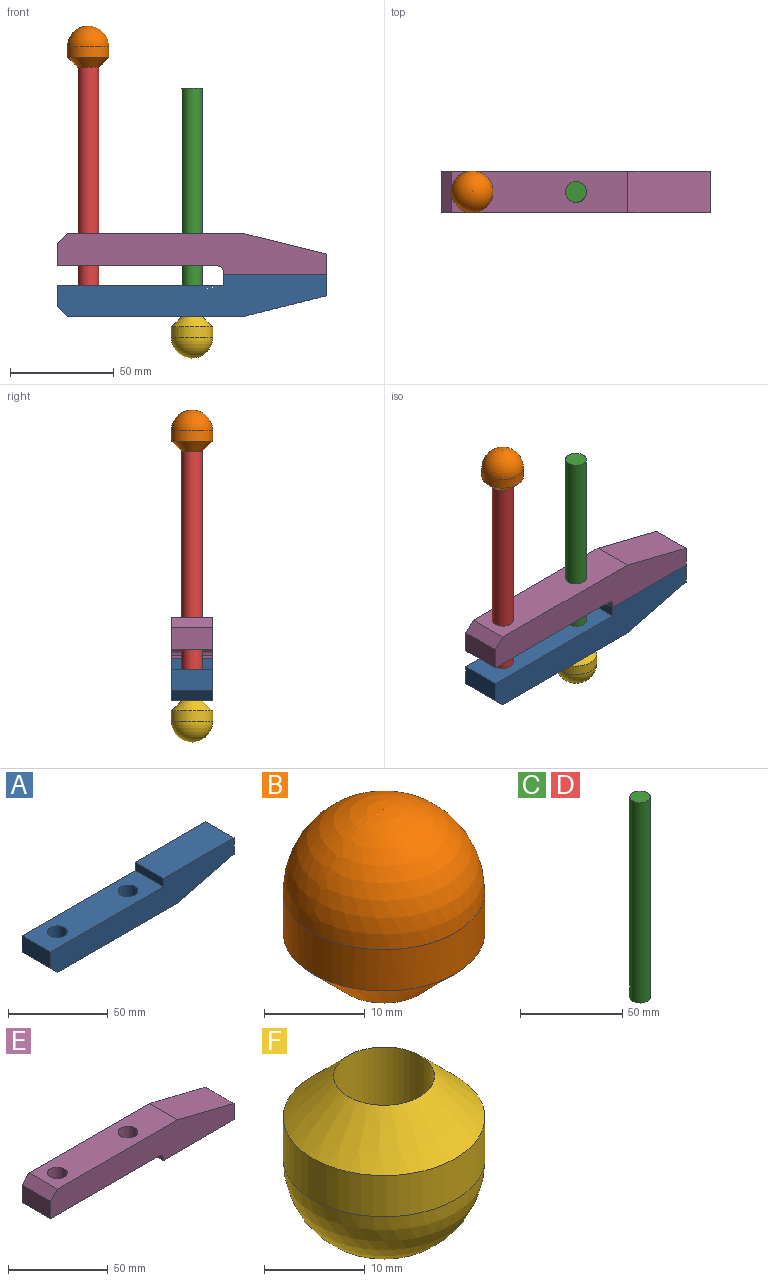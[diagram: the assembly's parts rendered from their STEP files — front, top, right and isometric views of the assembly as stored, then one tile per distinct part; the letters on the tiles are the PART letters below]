
ASSEMBLY  parts=6 mates=5
PART A: 13 faces, bbox 130x20x20 mm
  f0: plane 20x5mm, normal (-1,0,0), area 100mm2, adj f1,f7,f8,f9
  f1: plane 80x20mm, normal (0,0,1), area 1442.9mm2, adj f0,f2,f8,f9,f10,f11
  f2: plane 20x10mm, normal (-1,0,0), area 200mm2, adj f1,f3,f8,f9
  f3: plane 20x5mm, normal (-0.71,0,-0.71), area 141.4mm2, adj f2,f4,f8,f9
  f4: plane 85x20mm, normal (0,0,-1), area 1621.5mm2, adj f3,f5,f8,f9,f10
  f5: plane 40x20mm, normal (0.24,0,-0.97), area 824.6mm2, adj f4,f6,f8,f9
  f6: plane 20x10mm, normal (1,0,0), area 200mm2, adj f5,f7,f8,f9
  f7: plane 50x20mm, normal (0,0,1), area 1000mm2, adj f0,f6,f8,f9
  f8: plane 130x20mm, normal (0,-1,0), area 1987.5mm2, adj f0,f1,f2,f3,f4,f5,f6,f7
  f9: plane 130x20mm, normal (0,1,0), area 1987.5mm2, adj f0,f1,f2,f3,f4,f5,f6,f7
  f10: cylinder r=5mm len=15mm, axis (0,0,1), area 471.2mm2, adj f1,f4
  f11: cylinder r=5mm len=10mm, axis (0,0,1), area 314.2mm2, adj f1,f12
  f12: plane 10x10mm, normal (0,0,1), area 78.5mm2, adj f11
PART B: 5 faces, bbox 20x20x20 mm
  f0: cylinder r=10mm len=20mm, axis (0,0,-1), area 314.2mm2, adj f3,f4
  f1: cylinder r=5mm len=15mm, axis (0,0,-1), area 471.2mm2, adj f2,f4
  f2: plane 10x10mm, normal (0,0,-1), area 78.5mm2, adj f1
  f3: sphere r=10mm, area 628.3mm2, adj f0
  f4: cone r=10mm half-angle=45deg, axis (0,0,1), area 333.2mm2, adj f0,f1
PART C: 3 faces, bbox 10x10x120 mm
  f0: cylinder r=5mm len=120mm, axis (0,0,-1), area 3769.9mm2, adj f1,f2
  f1: plane 10x10mm, normal (0,0,1), area 78.5mm2, adj f0
  f2: plane 10x10mm, normal (0,0,-1), area 78.5mm2, adj f0
PART D: same geometry as C
PART E: 13 faces, bbox 130x20x20 mm
  f0: plane 20x10mm, normal (1,0,0), area 200mm2, adj f1,f7,f8,f9
  f1: plane 40x20mm, normal (0.24,0,0.97), area 824.6mm2, adj f0,f2,f8,f9
  f2: plane 85x20mm, normal (0,0,1), area 1542.9mm2, adj f1,f3,f8,f9,f11,f12
  f3: plane 20x5mm, normal (-0.71,0,0.71), area 141.4mm2, adj f2,f4,f8,f9
  f4: plane 20x10.66mm, normal (-1,0,0), area 213.1mm2, adj f3,f5,f8,f9
  f5: plane 77.5x20mm, normal (0,0,-1), area 1392.9mm2, adj f4,f8,f9,f10,f11,f12
  f6: plane 20x1.84mm, normal (-1,0,0), area 36.9mm2, adj f7,f8,f9,f10
  f7: plane 50x20mm, normal (0,0,-1), area 1000mm2, adj f0,f6,f8,f9
  f8: plane 130x20mm, normal (0,-1,0), area 2041.4mm2, adj f0,f1,f2,f3,f4,f5,f6,f7
  f9: plane 130x20mm, normal (0,1,0), area 2041.4mm2, adj f0,f1,f2,f3,f4,f5,f6,f7
  f10: cylinder r=2.5mm len=20mm, axis (0,-1,0), area 78.5mm2, adj f5,f6,f8,f9
  f11: cylinder r=5mm len=15.66mm, axis (0,0,-1), area 491.9mm2, adj f2,f5
  f12: cylinder r=5mm len=15.66mm, axis (0,0,-1), area 491.9mm2, adj f2,f5
PART F: 5 faces, bbox 20x20x20 mm
  f0: cylinder r=10mm len=20mm, axis (0,0,1), area 314.2mm2, adj f3,f4
  f1: cylinder r=5mm len=15mm, axis (0,0,1), area 471.2mm2, adj f2,f3
  f2: plane 10x10mm, normal (0,0,1), area 78.5mm2, adj f1
  f3: cone r=5mm half-angle=45deg, axis (0,0,-1), area 333.2mm2, adj f0,f1
  f4: sphere r=10mm, area 628.3mm2, adj f0
PLACE A t=(36.5,-30.74,114.43)mm
PLACE B t=(-13.5,-30.74,224.43)mm
PLACE C t=(73.99,-30.74,94.43)mm
PLACE D t=(23.99,-30.74,119.43)mm
PLACE E t=(36.5,-30.74,134.43)mm
PLACE F t=(36.5,-30.74,104.43)mm
MATE fastened A.f11 <-> D.f0  axis (0,0,1) through (-13.5,-30.74,119.43)mm
MATE fastened F.f0 <-> C.f0  axis (0,0,1) through (36.5,-30.74,94.43)mm
MATE slider F.f0 <-> A.f10  axis (0,0,-1) through (36.5,-30.74,104.43)mm
MATE slider E.f12 <-> D.f0  axis (0,0,1) through (-13.5,-30.74,144.43)mm
MATE fastened D.f0 <-> B.f1  axis (0,0,1) through (-13.5,-30.74,239.43)mm
